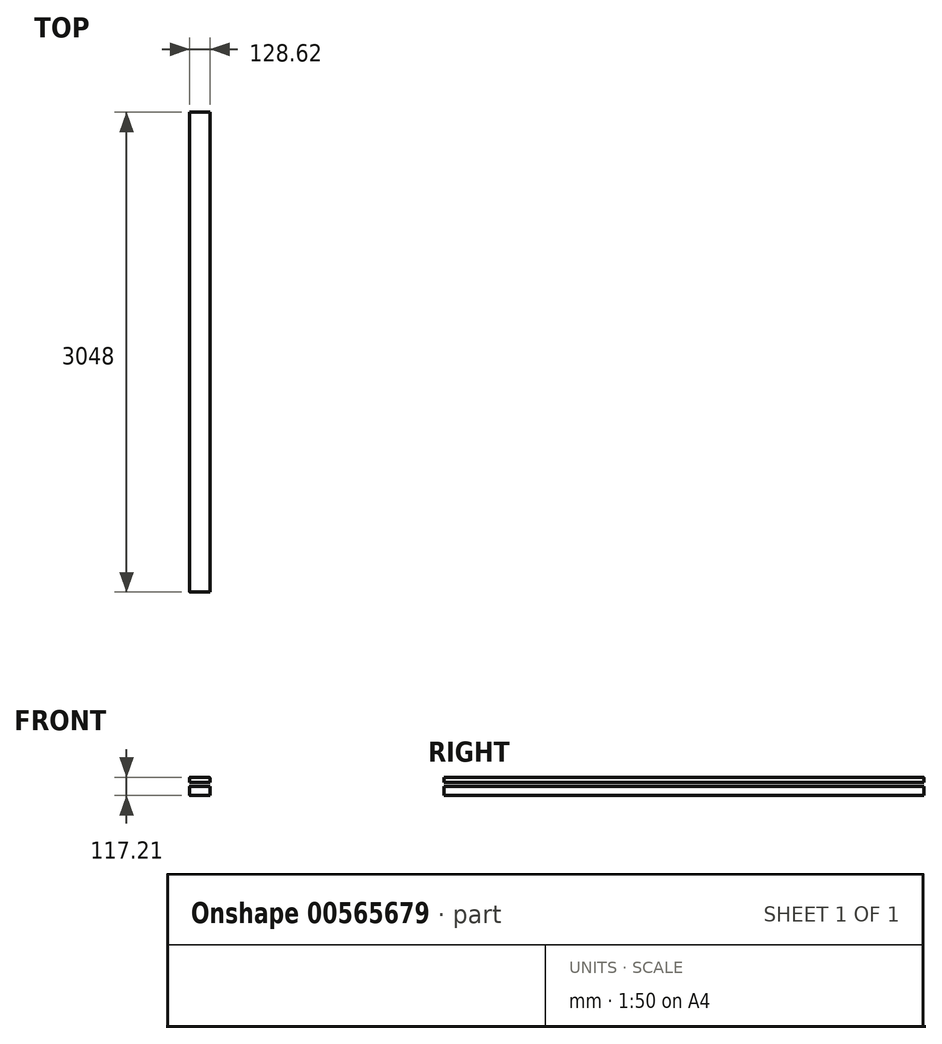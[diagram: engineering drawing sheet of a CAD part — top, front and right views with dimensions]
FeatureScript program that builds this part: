
annotation { "Feature Type Name" : "Feature", "Feature Type Description" : "" }
export const myFeature = defineFeature(function(context is Context, id is Id, definition is map)
    precondition{}
    {
        {
            var Q0;
            Q0=qCreatedBy(makeId("Front.planeOp"),FACE);
            var sketch = newSketch(context, id + "F0", { "sketchPlane" : qUnion([Q0])});
            skLineSegment(sketch, "E0.bottom", {"start": v(-53.37, 56.99) * mm, "end": v(75.25, 56.99) * mm});
            skLineSegment(sketch, "E0.top", {"start": v(-53.37, -60.22) * mm, "end": v(75.25, -60.22) * mm});
            skLineSegment(sketch, "E0.left", {"start": v(-53.37, 56.99) * mm, "end": v(-53.37, -60.22) * mm});
            skLineSegment(sketch, "E0.right", {"start": v(75.25, 56.99) * mm, "end": v(75.25, -60.22) * mm});
            skLineSegment(sketch, "E1", {"start": v(-53.37, 0) * mm, "end": v(75.25, 0) * mm});
            skPoint(sketch, "E1.startSnap0", {"position": v(-53.37, -1.62) * mm});
            skLineSegment(sketch, "E2", {"start": v(-53.37, 23.88) * mm, "end": v(75.25, 23.88) * mm});
            skSolve(sketch);
        }
        {
            var Q0;
            {var subQ0=sQuery(id+"F0.wireOp",EDGE,"E0.bottom");Q0=makeQuery(id+"F0.imprint","IMPRINT",FACE,{"disambiguationData":[TD([[makeQuery(id+"F0.imprint","IMPRINT",EDGE,{"derivedFrom":subQ0}),-1.0]])]});}
            var Q1;
            {var subQ0=sQuery(id+"F0.wireOp",EDGE,"E0.top");Q1=makeQuery(id+"F0.imprint","IMPRINT",FACE,{"disambiguationData":[TD([[makeQuery(id+"F0.imprint","IMPRINT",EDGE,{"derivedFrom":subQ0}),1.0]])]});}
            var Q2;
            Q2=sQuery(id+"F0.wireOp",EDGE,"E0.left");
            var Q3;
            Q3=sQuery(id+"F0.wireOp",EDGE,"E0.bottom");
            var Q4;
            Q4=sQuery(id+"F0.wireOp",EDGE,"E0.right");
            var Q5;
            Q5=sQuery(id+"F0.wireOp",EDGE,"E0.top");
            extrude(context, id + "F1", {"entities" : qUnion([Q0, Q1]), "surfaceEntities" : qUnion([Q2, Q3, Q4, Q5]), "depth" : 3048 * mm, "offsetDistance" : 30.48 * mm});
        }
        {
            var Q0;
            Q0=makeQuery(id+"F1.opExtrude","SWEPT_EDGE",EDGE,{"disambiguationData":[OSD([sQuery(id+"F0.wireOp",EDGE,"E0.bottom"),sQuery(id+"F0.wireOp",EDGE,"E0.left")])]});
            var Q1;
            Q1=makeQuery(id+"F1.opExtrude","SWEPT_EDGE",EDGE,{"disambiguationData":[OSD([sQuery(id+"F0.wireOp",EDGE,"E0.left"),sQuery(id+"F0.wireOp",EDGE,"E1")])]});
            var Q2;
            Q2=makeQuery(id+"F1.opExtrude","SWEPT_EDGE",EDGE,{"disambiguationData":[OSD([sQuery(id+"F0.wireOp",EDGE,"E0.top"),sQuery(id+"F0.wireOp",EDGE,"E0.left")])]});
            var Q3;
            {var subQ0=sQuery(id+"F0.wireOp",EDGE,"E0.left");Q3=makeQuery(id+"F1.opExtrude","CAP_EDGE",EDGE,{"disambiguationData":[OSD([subQ0]),TDD([makeQuery(id+"F0.imprint","IMPRINT",EDGE,{"disambiguationData":[TD([[makeQuery(id+"F0.imprint","INTERSECT",VERTEX,{"derivedFrom":[sQuery(id+"F0.wireOp",EDGE,"E0.top"),subQ0]}),1.0]])],"derivedFrom":subQ0})])],"isStart":true});}
            var Q4;
            Q4=makeQuery(id+"F1.opExtrude","CAP_EDGE",EDGE,{"disambiguationData":[OSD([sQuery(id+"F0.wireOp",EDGE,"E0.bottom")])],"isStart":true});
            var Q5;
            Q5=makeQuery(id+"F1.opExtrude","SWEPT_EDGE",EDGE,{"disambiguationData":[OSD([sQuery(id+"F0.wireOp",EDGE,"E0.bottom"),sQuery(id+"F0.wireOp",EDGE,"E0.right")])]});
            fillet(context, id + "F2", {"entities" : qUnion([Q0, Q1, Q2, Q3, Q4, Q5]), "radius" : 4.57 * mm, "tangentPropagation" : true, "allowEdgeOverflow" : false});
        }
    });
